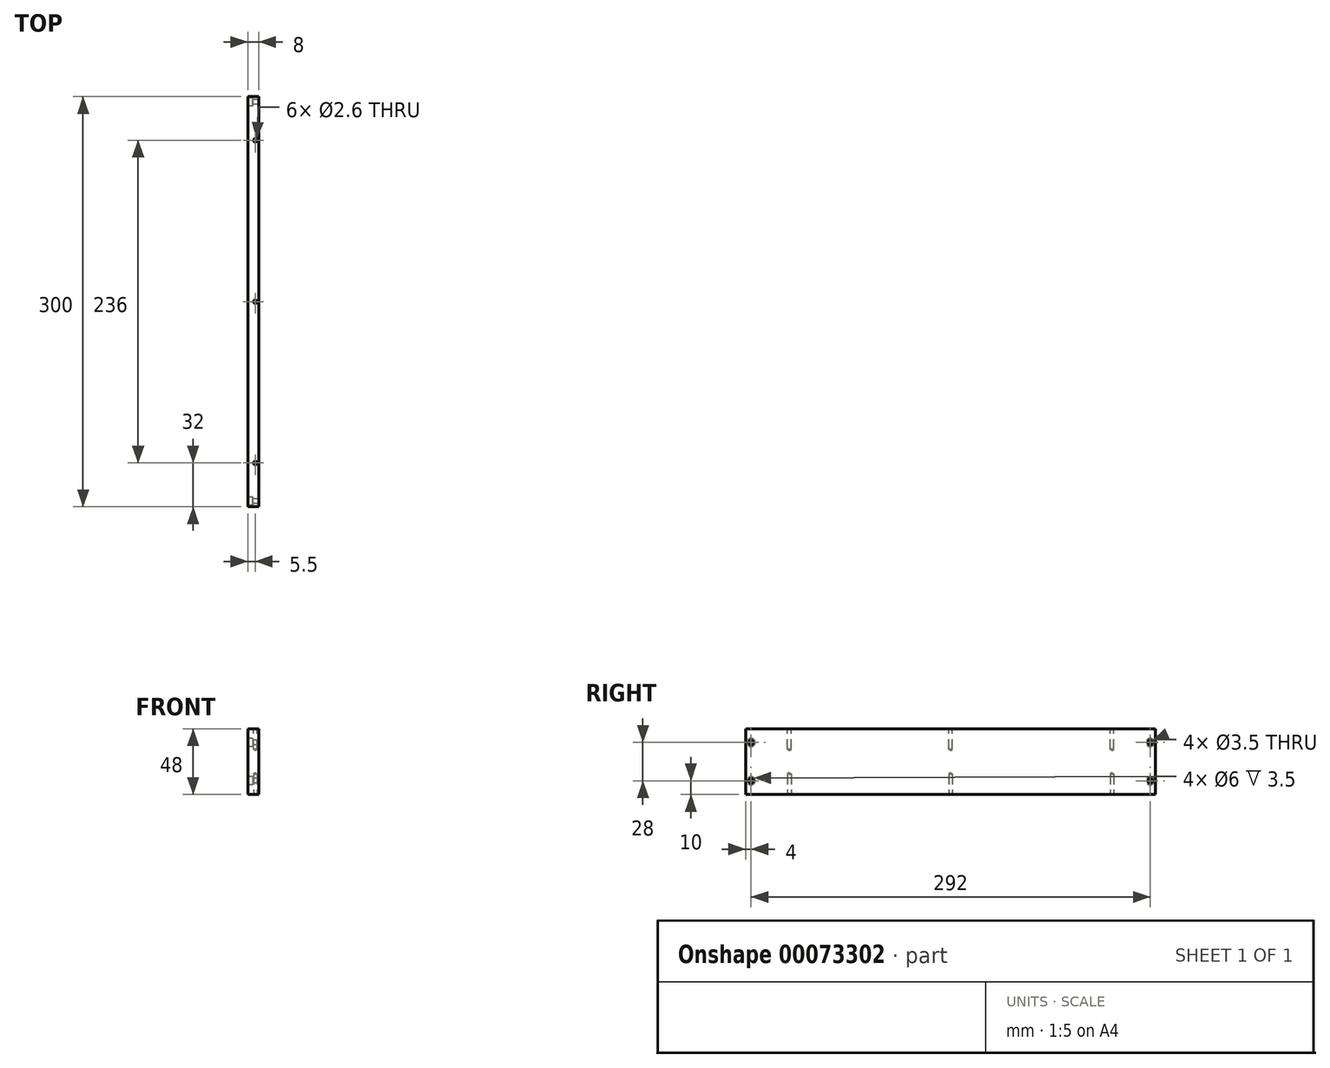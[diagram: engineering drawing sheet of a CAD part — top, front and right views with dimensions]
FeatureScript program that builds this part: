
annotation { "Feature Type Name" : "Feature", "Feature Type Description" : "" }
export const myFeature = defineFeature(function(context is Context, id is Id, definition is map)
    precondition{}
    {
        {
            var Q0;
            Q0=qCreatedBy(makeId("Front.planeOp"),FACE);
            var sketch = newSketch(context, id + "F0", { "sketchPlane" : qUnion([Q0])});
            skLineSegment(sketch, "E0.rect.bottom", {"start": v(-4, 24) * mm, "end": v(4, 24) * mm});
            skLineSegment(sketch, "E0.rect.top", {"start": v(-4, -24) * mm, "end": v(4, -24) * mm});
            skLineSegment(sketch, "E0.rect.left", {"start": v(-4, 24) * mm, "end": v(-4, -24) * mm});
            skLineSegment(sketch, "E0.rect.right", {"start": v(4, 24) * mm, "end": v(4, -24) * mm});
            skPoint(sketch, "E0.rect.middle", {"position": v(0, 0) * mm});
            skSolve(sketch);
        }
        {
            var Q0;
            Q0=makeQuery(id+"F0.imprint","IMPRINT",FACE,{"disambiguationData":[TD([[makeQuery(id+"F0.imprint","IMPRINT",EDGE,{"derivedFrom":sQuery(id+"F0.wireOp",EDGE,"E0.rect.bottom")}),-1.0]])]});
            extrude(context, id + "F1", {"entities" : qUnion([Q0]), "endBound" : BoundingType.SYMMETRIC, "depth" : 300 * mm});
        }
        {
            var Q0;
            Q0=makeQuery(id+"F1.opExtrude","SWEPT_FACE",FACE,{"disambiguationData":[OSD([sQuery(id+"F0.wireOp",EDGE,"E0.rect.bottom")])]});
            var sketch = newSketch(context, id + "F2", { "sketchPlane" : qUnion([Q0])});
            skPoint(sketch, "E1", {"position": v(1.5, -118) * mm});
            skPoint(sketch, "E2", {"position": v(1.5, 0) * mm});
            skPoint(sketch, "E3", {"position": v(1.5, 118) * mm});
            skSolve(sketch);
        }
        {
            var Q0;
            Q0=makeQuery(id+"F1.opExtrude","SWEPT_FACE",FACE,{"disambiguationData":[OSD([sQuery(id+"F0.wireOp",EDGE,"E0.rect.top")])]});
            var sketch = newSketch(context, id + "F3", { "sketchPlane" : qUnion([Q0])});
            skPoint(sketch, "E4", {"position": v(1.5, -118) * mm});
            skPoint(sketch, "E5", {"position": v(1.5, 0) * mm});
            skPoint(sketch, "E6", {"position": v(1.5, 118) * mm});
            skSolve(sketch);
        }
        {
            var Q0;
            Q0=sQuery(id+"F3.wireOp",VERTEX,"E4");
            var Q1;
            Q1=sQuery(id+"F3.wireOp",VERTEX,"E5");
            var Q2;
            Q2=sQuery(id+"F3.wireOp",VERTEX,"E6");
            var Q3;
            Q3=sQuery(id+"F2.wireOp",VERTEX,"E1");
            var Q4;
            Q4=sQuery(id+"F2.wireOp",VERTEX,"E2");
            var Q5;
            Q5=sQuery(id+"F2.wireOp",VERTEX,"E3");
            var Q6;
            Q6=makeQuery(id+"F1.opExtrude","SWEPT_BODY",BODY,{"disambiguationData":[OSD([sQuery(id+"F0.wireOp",EDGE,"E0.rect.bottom"),sQuery(id+"F0.wireOp",EDGE,"E0.rect.top"),sQuery(id+"F0.wireOp",EDGE,"E0.rect.left"),sQuery(id+"F0.wireOp",EDGE,"E0.rect.right")])]});
            hole(context, id + "F4", {"style" : HoleStyle.SIMPLE, "holeDiameter" : 2.6 * mm, "endStyle" : HoleEndStyle.BLIND, "holeDepth" : 15 * mm, "locations" : qUnion([Q0, Q1, Q2, Q3, Q4, Q5]), "scope" : qUnion([Q6]), "tappedDepth" : 12 * mm, "tapClearance" : 3});
        }
        {
            var Q0;
            Q0=makeQuery(id+"F1.opExtrude","SWEPT_FACE",FACE,{"disambiguationData":[OSD([sQuery(id+"F0.wireOp",EDGE,"E0.rect.left")])]});
            var sketch = newSketch(context, id + "F5", { "sketchPlane" : qUnion([Q0])});
            skPoint(sketch, "E7", {"position": v(-146, 14) * mm});
            skPoint(sketch, "E8.MirrorP", {"position": v(146, 14) * mm});
            skPoint(sketch, "E9.MirrorP", {"position": v(-146, -14) * mm});
            skPoint(sketch, "E10.MirrorP", {"position": v(146, -14) * mm});
            skSolve(sketch);
        }
        {
            var Q0;
            Q0=sQuery(id+"F5.wireOp",VERTEX,"E8.MirrorP");
            var Q1;
            Q1=sQuery(id+"F5.wireOp",VERTEX,"E10.MirrorP");
            var Q2;
            Q2=sQuery(id+"F5.wireOp",VERTEX,"E9.MirrorP");
            var Q3;
            Q3=sQuery(id+"F5.wireOp",VERTEX,"E7");
            var Q4;
            Q4=makeQuery(id+"F1.opExtrude","SWEPT_BODY",BODY,{"disambiguationData":[OSD([sQuery(id+"F0.wireOp",EDGE,"E0.rect.bottom"),sQuery(id+"F0.wireOp",EDGE,"E0.rect.top"),sQuery(id+"F0.wireOp",EDGE,"E0.rect.left"),sQuery(id+"F0.wireOp",EDGE,"E0.rect.right")])]});
            hole(context, id + "F6", {"style" : HoleStyle.C_BORE, "holeDiameter" : 3.5 * mm, "cBoreDiameter" : 6 * mm, "cBoreDepth" : 3.5 * mm, "endStyle" : HoleEndStyle.THROUGH, "locations" : qUnion([Q0, Q1, Q2, Q3]), "scope" : qUnion([Q4]), "tappedDepth" : 12 * mm, "tapClearance" : 3});
        }
    });
